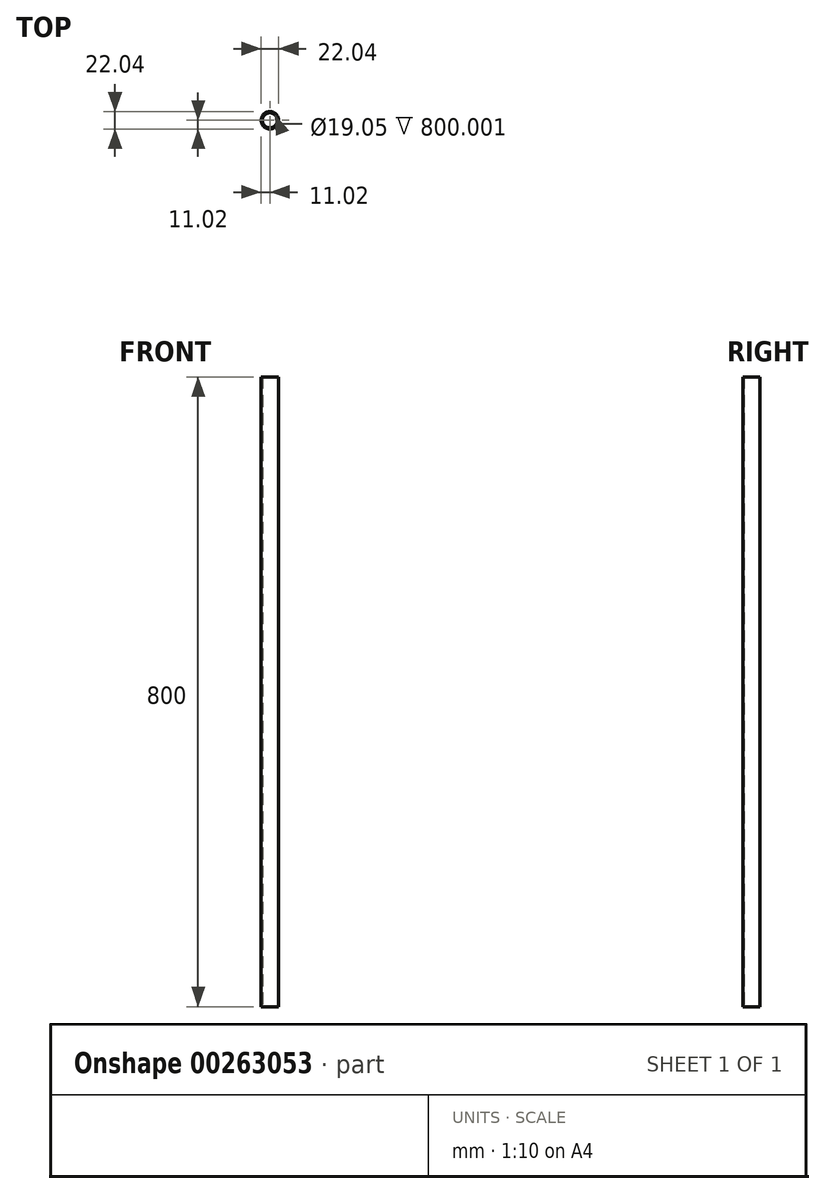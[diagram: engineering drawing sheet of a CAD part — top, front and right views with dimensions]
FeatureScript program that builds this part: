
annotation { "Feature Type Name" : "Feature", "Feature Type Description" : "" }
export const myFeature = defineFeature(function(context is Context, id is Id, definition is map)
    precondition{}
    {
        {
            var Q0;
            Q0=qCreatedBy(makeId("Top.planeOp"),FACE);
            var sketch = newSketch(context, id + "F0", { "sketchPlane" : qUnion([Q0])});
            skCircle(sketch, "E0", {"center": v(0, 0) * mm, "radius": 9.53 * mm});
            skCircle(sketch, "E1", {"center": v(0, 0) * mm, "radius": 11.02 * mm});
            skSolve(sketch);
        }
        {
            var Q0;
            Q0=makeQuery(id+"F0.imprint","IMPRINT",FACE,{"disambiguationData":[TD([[makeQuery(id+"F0.imprint","IMPRINT",EDGE,{"derivedFrom":sQuery(id+"F0.wireOp",EDGE,"E0")}),-1.0]])]});
            var Q1;
            Q1=sQuery(id+"F0.wireOp",EDGE,"E0");
            extrude(context, id + "F1", {"entities" : qUnion([Q0]), "surfaceEntities" : qUnion([Q1]), "depth" : 800 * mm});
        }
    });
